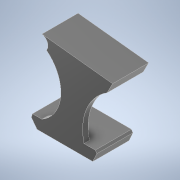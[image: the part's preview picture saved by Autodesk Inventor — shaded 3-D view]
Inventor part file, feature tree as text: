
AUTODESK INVENTOR PART (.ipt)
format: ipt  version: 2022 (Build 260153000, 153)  size: 290,816 bytes
history: native  units: in
note: dims shown in document units (in); Inventor stores cm internally (conversion verified against a paired STEP export)
features: extrude x2, other x1, sketch x1
ambient origin geometry x8: Origin, YZ Plane, XZ Plane, XY Plane, X Axis, Y Axis, Z Axis, Center Point
bodies: Body1 (feature_tree)
feature tree (4):
  other  "Sólido1"
  extrude  "Extrusión1"  Depth=0.0394in TaperAngle=0.0deg
  extrude  "Extrusión3"  Depth=0.0787in
  sketch  "Boceto3"  dims[d3=0.2559in d4=0.0in d7=0.0394in d8=0.0in d9=0.0787in d10=0.0787in]
